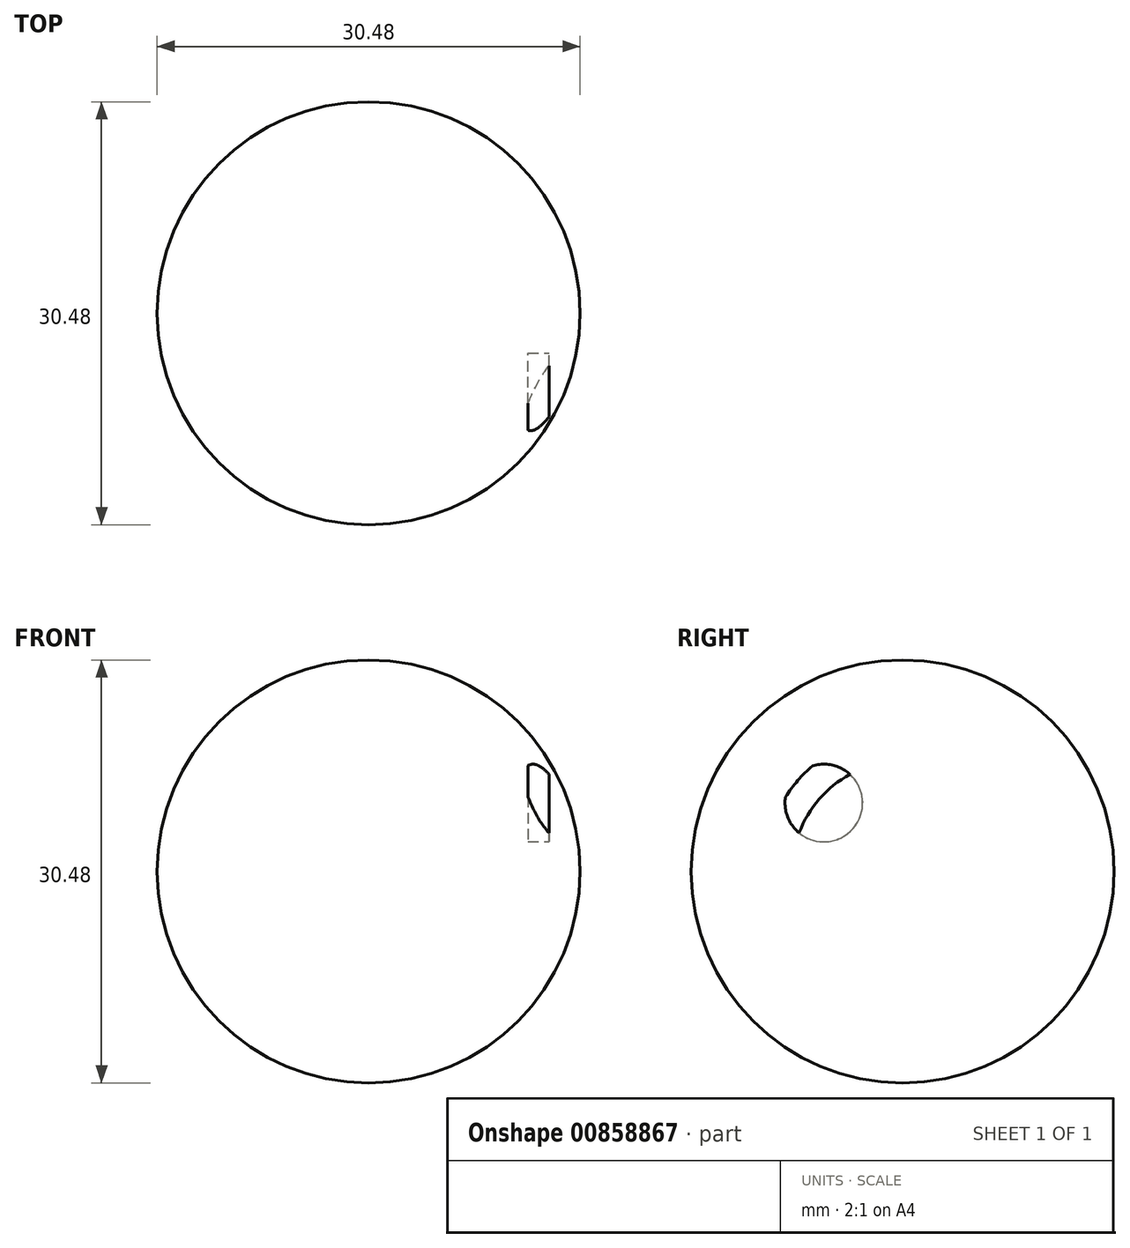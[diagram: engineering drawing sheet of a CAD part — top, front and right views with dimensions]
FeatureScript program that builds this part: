
annotation { "Feature Type Name" : "Feature", "Feature Type Description" : "" }
export const myFeature = defineFeature(function(context is Context, id is Id, definition is map)
    precondition{}
    {
        {
            var Q0;
            Q0=qCreatedBy(makeId("Front.planeOp"),FACE);
            var sketch = newSketch(context, id + "F0", { "sketchPlane" : qUnion([Q0])});
            skArc(sketch, "E0", {"start": v(0, -15.24) * mm, "mid": v(15.24, 0) * mm, "end": v(0, 15.24) * mm});
            skLineSegment(sketch, "E1", {"start": v(0, 15.24) * mm, "end": v(0, -15.24) * mm});
            skSolve(sketch);
        }
        {
            var Q0;
            Q0=makeQuery(id+"F0.imprint","IMPRINT",FACE,{"disambiguationData":[TD([[makeQuery(id+"F0.imprint","IMPRINT",EDGE,{"derivedFrom":sQuery(id+"F0.wireOp",EDGE,"E0")}),1.0]])]});
            var Q1;
            Q1=sQuery(id+"F0.wireOp",EDGE,"E1");
            revolve(context, id + "F1", {"surfaceOperationType" : NewSurfaceOperationType.NEW, "entities" : qUnion([Q0]), "axis" : qUnion([Q1]), "revolveType" : RevolveType.FULL});
        }
        {
            var Q0;
            Q0=qCreatedBy(makeId("Right.planeOp"),FACE);
            cPlane(context, id + "F2", {"entities" : qUnion([Q0]), "cplaneType" : CPlaneType.OFFSET, "offset" : 13 * mm, "width" : 150 * mm, "height" : 150 * mm});
        }
        {
            var Q0;
            Q0=qCreatedBy(id+"F2.planeOp",FACE);
            var sketch = newSketch(context, id + "F3", { "sketchPlane" : qUnion([Q0])});
            skCircle(sketch, "E2", {"center": v(-5.68, 4.93) * mm, "radius": 2.8 * mm});
            skCircle(sketch, "E3.MirrorC", {"center": v(5.68, 4.93) * mm, "radius": 2.8 * mm});
            skSolve(sketch);
        }
        {
            var Q0;
            Q0=makeQuery(id+"F3.imprint","IMPRINT",FACE,{"disambiguationData":[TD([[makeQuery(id+"F3.imprint","IMPRINT",EDGE,{"derivedFrom":sQuery(id+"F3.wireOp",EDGE,"E2")}),1.0]])]});
            var Q1;
            Q1=makeQuery(id+"F3.imprint","IMPRINT",FACE,{"disambiguationData":[TD([[makeQuery(id+"F3.imprint","IMPRINT",EDGE,{"derivedFrom":sQuery(id+"F3.wireOp",EDGE,"E3.MirrorC")}),-1.0]])]});
            extrude(context, id + "F4", {"entities" : qUnion([Q0, Q1]), "operationType" : NewBodyOperationType.REMOVE, "oppositeDirection" : true, "depth" : 1.5 * mm, "offsetDistance" : 25 * mm});
        }
        {
            var Q0;
            Q0=makeQuery(id+"F1.opRevolve","SWEPT_BODY",BODY,{"disambiguationData":[OSD([sQuery(id+"F0.wireOp",EDGE,"E0"),sQuery(id+"F0.wireOp",EDGE,"E1")])]});
            transform(context, id + "F5", {"entities" : qUnion([Q0]), "transformType" : TransformType.TRANSLATION_3D, "dx" : 0 * mm, "dy" : 0 * mm, "dz" : 0 * mm, "makeCopy" : true});
        }
    });
